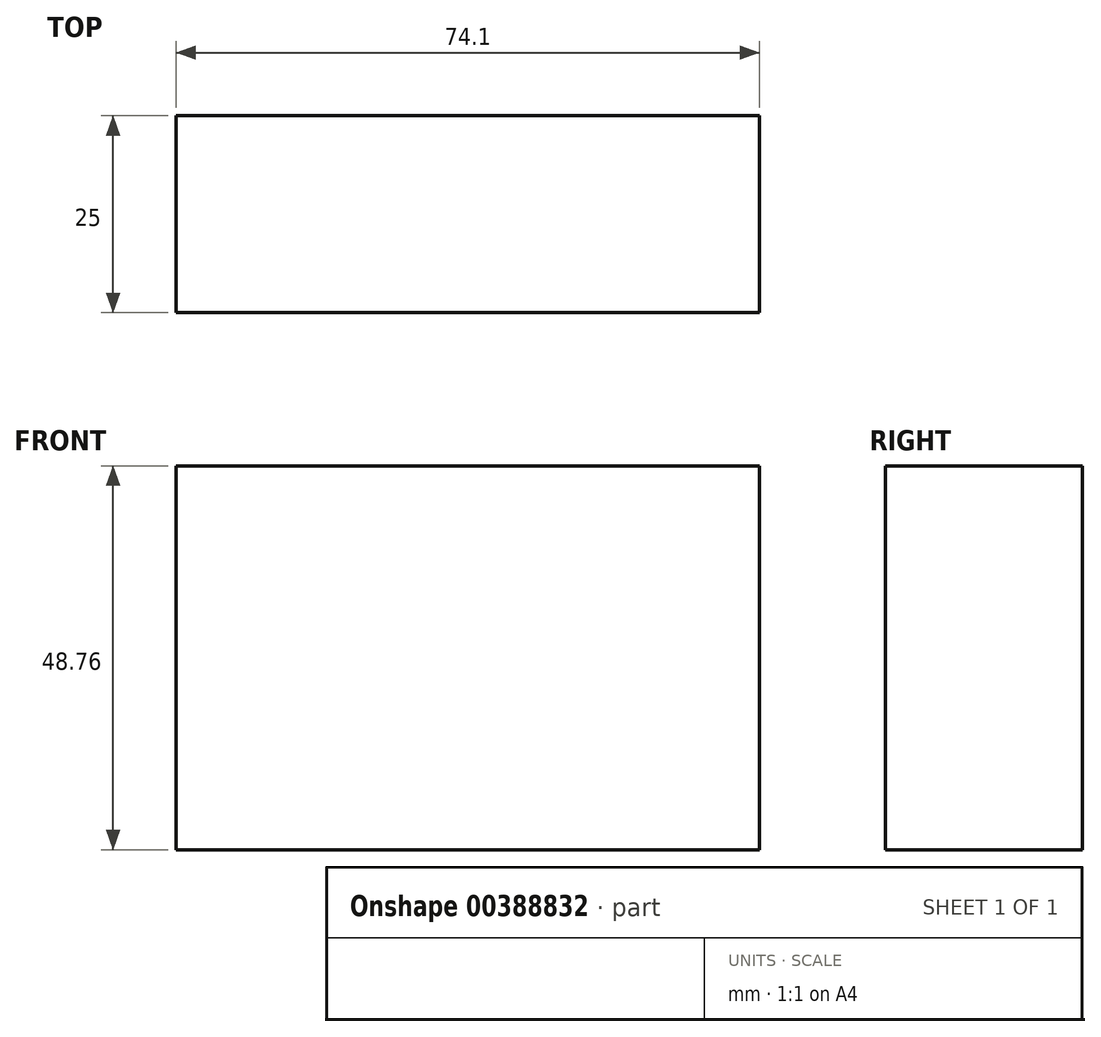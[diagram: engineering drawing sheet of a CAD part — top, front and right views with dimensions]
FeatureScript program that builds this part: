
annotation { "Feature Type Name" : "Feature", "Feature Type Description" : "" }
export const myFeature = defineFeature(function(context is Context, id is Id, definition is map)
    precondition{}
    {
        {
            var Q0;
            Q0=qCreatedBy(makeId("Front.planeOp"),FACE);
            var sketch = newSketch(context, id + "F0", { "sketchPlane" : qUnion([Q0])});
            skLineSegment(sketch, "E0.bottom", {"start": v(-115.5, 18.73) * mm, "end": v(-41.39, 18.73) * mm});
            skLineSegment(sketch, "E0.top", {"start": v(-115.5, 67.5) * mm, "end": v(-41.39, 67.5) * mm});
            skLineSegment(sketch, "E0.left", {"start": v(-115.5, 18.73) * mm, "end": v(-115.5, 67.5) * mm});
            skLineSegment(sketch, "E0.right", {"start": v(-41.39, 18.73) * mm, "end": v(-41.39, 67.5) * mm});
            skPoint(sketch, "E0.middle", {"position": v(-78.44, 43.11) * mm});
            skSolve(sketch);
        }
        {
            var Q0;
            Q0=makeQuery(id+"F0.imprint","IMPRINT",FACE,{"disambiguationData":[TD([[makeQuery(id+"F0.imprint","IMPRINT",EDGE,{"derivedFrom":sQuery(id+"F0.wireOp",EDGE,"E0.bottom")}),1.0]])]});
            extrude(context, id + "F1", {"entities" : qUnion([Q0]), "depth" : 25 * mm});
        }
    });
